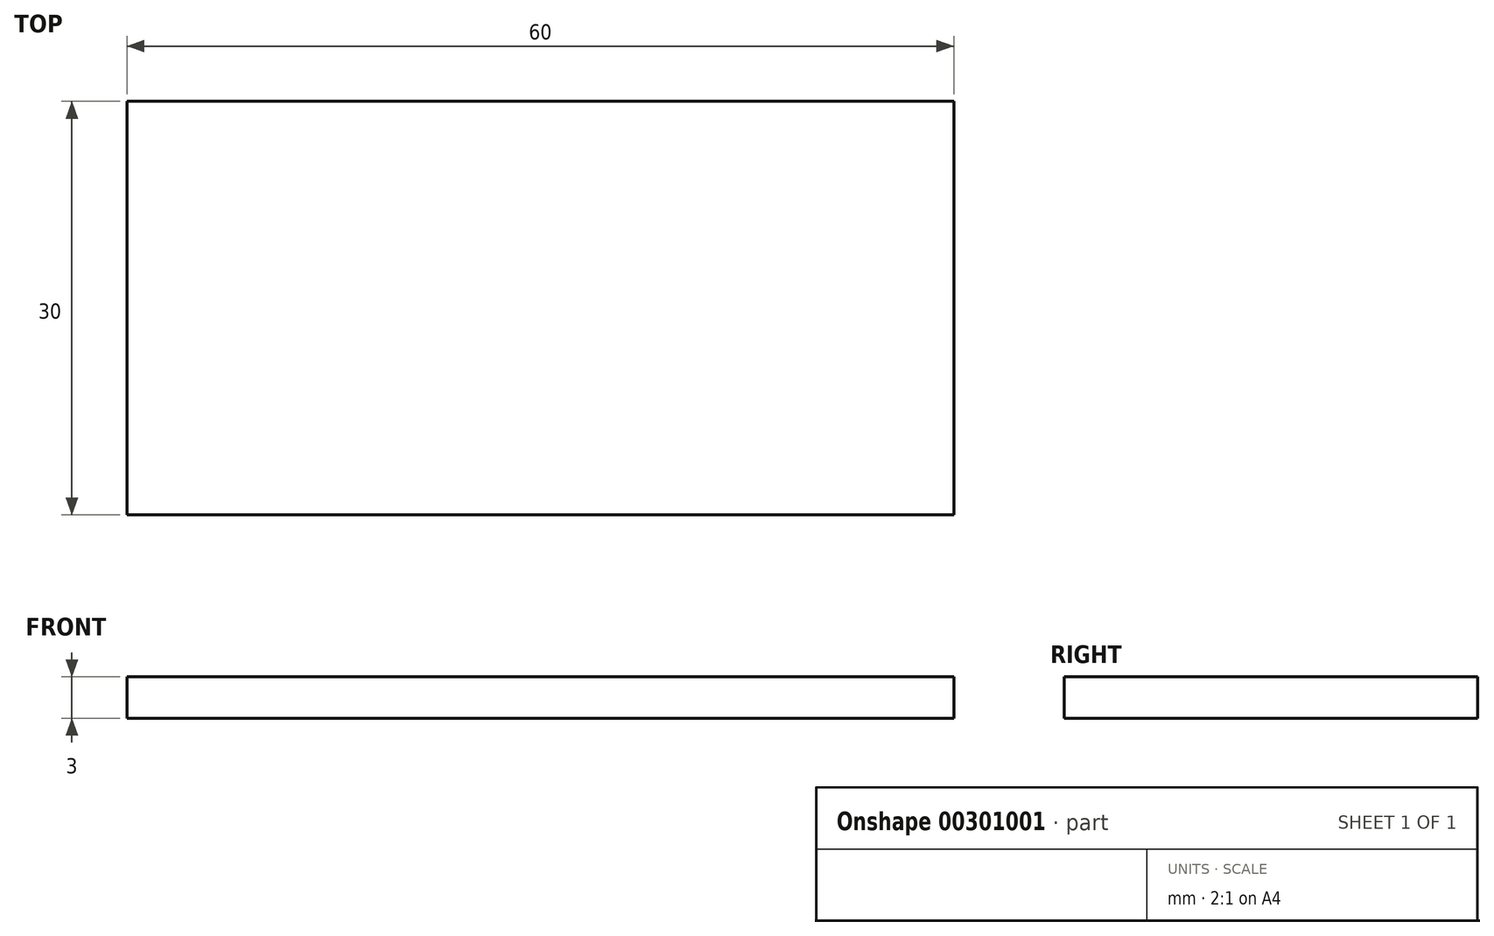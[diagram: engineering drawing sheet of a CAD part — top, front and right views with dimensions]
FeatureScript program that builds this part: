
annotation { "Feature Type Name" : "Feature", "Feature Type Description" : "" }
export const myFeature = defineFeature(function(context is Context, id is Id, definition is map)
    precondition{}
    {
        {
            var Q0;
            Q0=qCreatedBy(makeId("Top.planeOp"),FACE);
            var sketch = newSketch(context, id + "F0", { "sketchPlane" : qUnion([Q0])});
            skLineSegment(sketch, "E0", {"start": v(-36.56, 18.45) * mm, "end": v(-36.56, -11.55) * mm});
            skLineSegment(sketch, "E1", {"start": v(-36.56, -11.55) * mm, "end": v(23.44, -11.55) * mm});
            skLineSegment(sketch, "E2", {"start": v(23.44, -11.55) * mm, "end": v(23.44, 18.45) * mm});
            skLineSegment(sketch, "E3", {"start": v(23.44, 18.45) * mm, "end": v(-36.56, 18.45) * mm});
            skSolve(sketch);
        }
        {
            var Q0;
            Q0=makeQuery(id+"F0.imprint","IMPRINT",FACE,{"disambiguationData":[TD([[makeQuery(id+"F0.imprint","IMPRINT",EDGE,{"derivedFrom":sQuery(id+"F0.wireOp",EDGE,"E0")}),1.0]])]});
            extrude(context, id + "F1", {"entities" : qUnion([Q0]), "depth" : 3 * mm, "offsetDistance" : 25 * mm});
        }
    });
